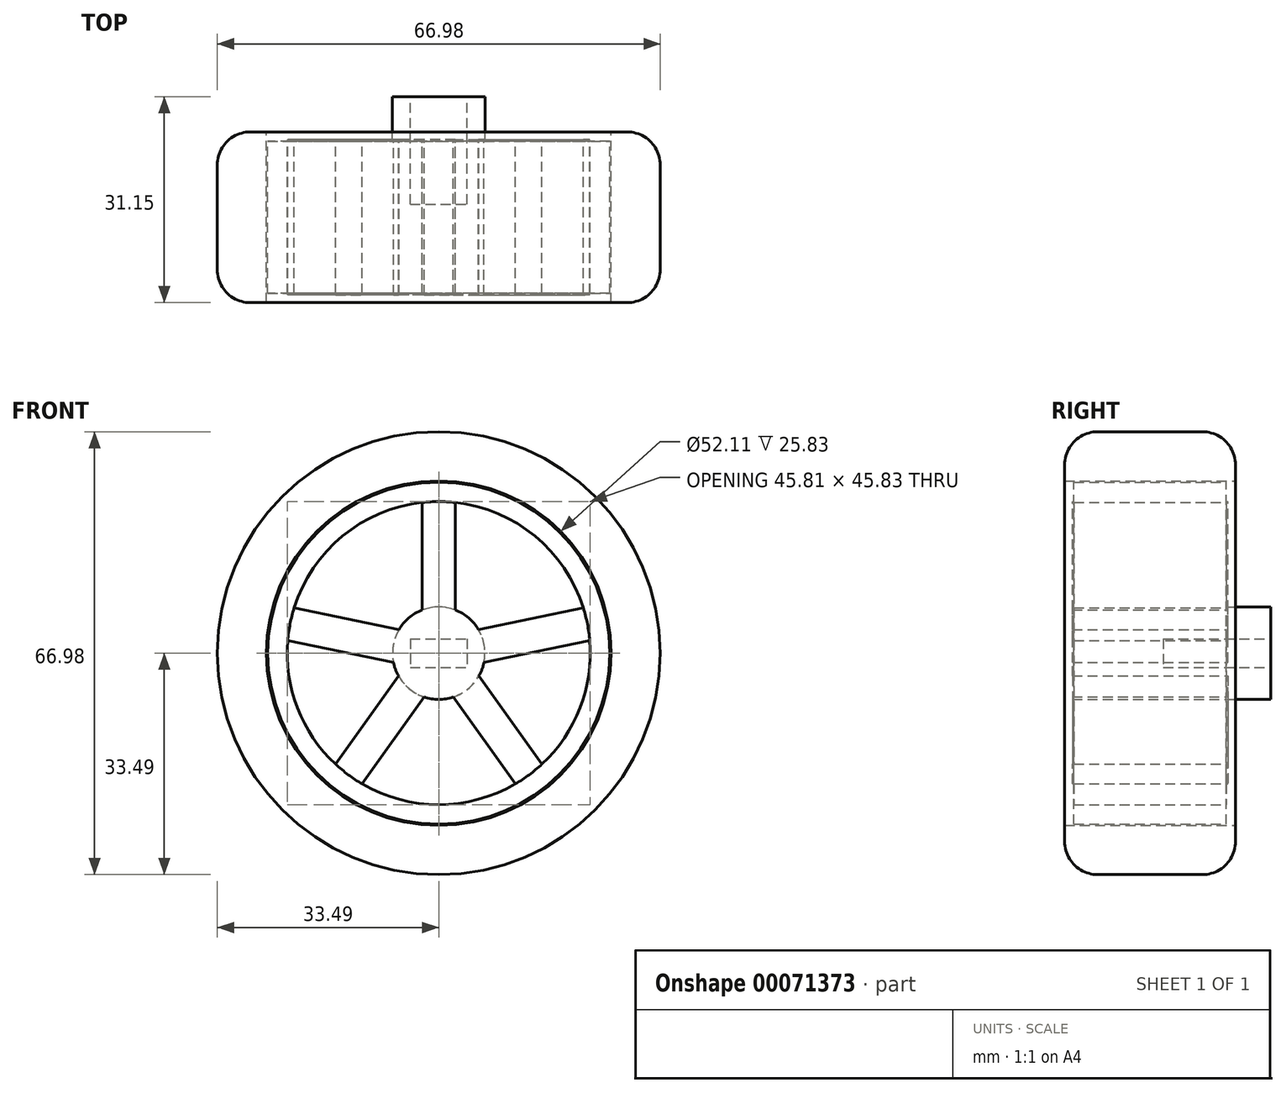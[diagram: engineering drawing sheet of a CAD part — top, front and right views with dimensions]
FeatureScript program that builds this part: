
annotation { "Feature Type Name" : "Feature", "Feature Type Description" : "" }
export const myFeature = defineFeature(function(context is Context, id is Id, definition is map)
    precondition{}
    {
        {
            var Q0;
            Q0=qCreatedBy(makeId("Front.planeOp"),FACE);
            var sketch = newSketch(context, id + "F0", { "sketchPlane" : qUnion([Q0])});
            skCircle(sketch, "E0", {"center": v(0, 0) * mm, "radius": 33.5 * mm});
            skCircle(sketch, "E1", {"center": v(0, 0) * mm, "radius": 26.06 * mm});
            skSolve(sketch);
        }
        {
            var Q0;
            Q0=makeQuery(id+"F0.imprint","IMPRINT",FACE,{"disambiguationData":[TD([[makeQuery(id+"F0.imprint","IMPRINT",EDGE,{"derivedFrom":sQuery(id+"F0.wireOp",EDGE,"E0")}),1.0]])]});
            extrude(context, id + "F1", {"entities" : qUnion([Q0]), "depth" : 25.83 * mm, "symmetric" : true});
        }
        {
            var Q0;
            Q0=qCreatedBy(makeId("Front.planeOp"),FACE);
            var sketch = newSketch(context, id + "F2", { "sketchPlane" : qUnion([Q0])});
            skCircle(sketch, "E2", {"center": v(0, 0) * mm, "radius": 25.86 * mm});
            skCircle(sketch, "E3", {"center": v(0, 0) * mm, "radius": 22.92 * mm});
            skSolve(sketch);
        }
        {
            var Q0;
            Q0 = qSketchRegion(id + "F2", true);
            extrude(context, id + "F3", {"entities" : qUnion([Q0]), "depth" : 23 * mm, "symmetric" : true});
        }
        {
            var Q0;
            Q0=qCreatedBy(makeId("Front.planeOp"),FACE);
            var sketch = newSketch(context, id + "F4", { "sketchPlane" : qUnion([Q0])});
            skCircle(sketch, "E4", {"center": v(0, 0) * mm, "radius": 6.99 * mm});
            skCircle(sketch, "E5", {"center": v(0, 0) * mm, "radius": 22.92 * mm});
            skLineSegment(sketch, "E6", {"start": v(-2.5, 6.52) * mm, "end": v(-2.5, 22.78) * mm});
            skLineSegment(sketch, "E7", {"start": v(2.5, 6.52) * mm, "end": v(2.5, 22.78) * mm});
            skLineSegment(sketch, "E8", {"start": v(2.2, -6.63) * mm, "end": v(11.58, -19.77) * mm});
            skLineSegment(sketch, "E9", {"start": v(6.07, -3.46) * mm, "end": v(15.6, -16.79) * mm});
            skLineSegment(sketch, "E10", {"start": v(6.02, 3.53) * mm, "end": v(21.87, 6.84) * mm});
            skLineSegment(sketch, "E11", {"start": v(6.84, -1.4) * mm, "end": v(22.83, 1.93) * mm});
            skLineSegment(sketch, "E12", {"start": v(0, 22.92) * mm, "end": v(0, -22.92) * mm, "construction": true});
            skLineSegment(sketch, "E13.MirrorCS", {"start": v(-6.02, 3.53) * mm, "end": v(-21.87, 6.84) * mm});
            skLineSegment(sketch, "E14.MirrorCS", {"start": v(-6.84, -1.4) * mm, "end": v(-22.83, 1.93) * mm});
            skLineSegment(sketch, "E15.MirrorCS", {"start": v(-6.07, -3.46) * mm, "end": v(-15.6, -16.79) * mm});
            skLineSegment(sketch, "E16.MirrorCS", {"start": v(-2.2, -6.63) * mm, "end": v(-11.58, -19.77) * mm});
            skSolve(sketch);
        }
        {
            var Q0;
            {var subQ0=sQuery(id+"F4.wireOp",EDGE,"E13.MirrorCS");Q0=makeQuery(id+"F4.imprint","IMPRINT",FACE,{"disambiguationData":[TD([[makeQuery(id+"F4.imprint","IMPRINT",EDGE,{"derivedFrom":subQ0}),1.0]])]});}
            var Q1;
            {var subQ0=sQuery(id+"F4.wireOp",EDGE,"E15.MirrorCS");Q1=makeQuery(id+"F4.imprint","IMPRINT",FACE,{"disambiguationData":[TD([[makeQuery(id+"F4.imprint","IMPRINT",EDGE,{"derivedFrom":subQ0}),1.0]])]});}
            var Q2;
            {var subQ0=sQuery(id+"F4.wireOp",EDGE,"E8");Q2=makeQuery(id+"F4.imprint","IMPRINT",FACE,{"disambiguationData":[TD([[makeQuery(id+"F4.imprint","IMPRINT",EDGE,{"derivedFrom":subQ0}),1.0]])]});}
            var Q3;
            {var subQ0=sQuery(id+"F4.wireOp",EDGE,"E7");Q3=makeQuery(id+"F4.imprint","IMPRINT",FACE,{"disambiguationData":[TD([[makeQuery(id+"F4.imprint","IMPRINT",EDGE,{"derivedFrom":subQ0}),1.0]])]});}
            var Q4;
            {var subQ0=sQuery(id+"F4.wireOp",EDGE,"E10");Q4=makeQuery(id+"F4.imprint","IMPRINT",FACE,{"disambiguationData":[TD([[makeQuery(id+"F4.imprint","IMPRINT",EDGE,{"derivedFrom":subQ0}),-1.0]])]});}
            extrude(context, id + "F5", {"entities" : qUnion([Q0, Q1, Q2, Q3, Q4]), "operationType" : NewBodyOperationType.ADD, "depth" : 23.5 * mm, "symmetric" : true});
        }
        {
            var Q0;
            Q0=qCreatedBy(makeId("Front.planeOp"),FACE);
            var sketch = newSketch(context, id + "F6", { "sketchPlane" : qUnion([Q0])});
            skCircle(sketch, "E17", {"center": v(0, 0) * mm, "radius": 6.99 * mm});
            skLineSegment(sketch, "E18.bottom", {"start": v(-4.3, 2.16) * mm, "end": v(4.3, 2.16) * mm});
            skLineSegment(sketch, "E18.top", {"start": v(-4.3, -2.16) * mm, "end": v(4.3, -2.16) * mm});
            skLineSegment(sketch, "E18.left", {"start": v(-4.3, 2.16) * mm, "end": v(-4.3, -2.16) * mm});
            skLineSegment(sketch, "E18.right", {"start": v(4.3, 2.16) * mm, "end": v(4.3, -2.16) * mm});
            skSolve(sketch);
        }
        {
            var Q0;
            Q0=makeQuery(id+"F6.imprint","IMPRINT",FACE,{"disambiguationData":[TD([[makeQuery(id+"F6.imprint","IMPRINT",EDGE,{"derivedFrom":sQuery(id+"F6.wireOp",EDGE,"E17")}),1.0]])]});
            extrude(context, id + "F7", {"entities" : qUnion([Q0]), "depth" : 11.75 * mm});
        }
        {
            var Q0;
            Q0=makeQuery(id+"F7.opExtrude","CAP_FACE",FACE,{"disambiguationData":[OSD([sQuery(id+"F6.wireOp",EDGE,"E17")])],"isStart":true});
            extrude(context, id + "F8", {"entities" : qUnion([Q0]), "operationType" : NewBodyOperationType.ADD, "depth" : 18.23 * mm});
        }
        {
            var Q0;
            Q0=makeQuery(id+"F6.imprint","IMPRINT",FACE,{"disambiguationData":[TD([[makeQuery(id+"F6.imprint","IMPRINT",EDGE,{"derivedFrom":sQuery(id+"F6.wireOp",EDGE,"E18.bottom")}),-1.0]])]});
            extrude(context, id + "F9", {"entities" : qUnion([Q0]), "operationType" : NewBodyOperationType.ADD, "depth" : 11.75 * mm});
        }
        {
            var Q0;
            Q0=makeQuery(id+"F9.opExtrude","CAP_FACE",FACE,{"disambiguationData":[OSD([sQuery(id+"F6.wireOp",EDGE,"E18.bottom"),sQuery(id+"F6.wireOp",EDGE,"E18.top"),sQuery(id+"F6.wireOp",EDGE,"E18.left"),sQuery(id+"F6.wireOp",EDGE,"E18.right")])],"isStart":true});
            extrude(context, id + "F10", {"entities" : qUnion([Q0]), "operationType" : NewBodyOperationType.ADD, "depth" : 2 * mm});
        }
        {
            var Q0;
            Q0=makeQuery(id+"F1.opExtrude","CAP_EDGE",EDGE,{"disambiguationData":[OSD([sQuery(id+"F0.wireOp",EDGE,"E0")])],"isStart":false});
            var Q1;
            Q1=makeQuery(id+"F1.opExtrude","CAP_EDGE",EDGE,{"disambiguationData":[OSD([sQuery(id+"F0.wireOp",EDGE,"E0")])],"isStart":true});
            fillet(context, id + "F11", {"entities" : qUnion([Q0, Q1]), "radius" : 5 * mm, "tangentPropagation" : true, "allowEdgeOverflow" : false});
        }
    });
